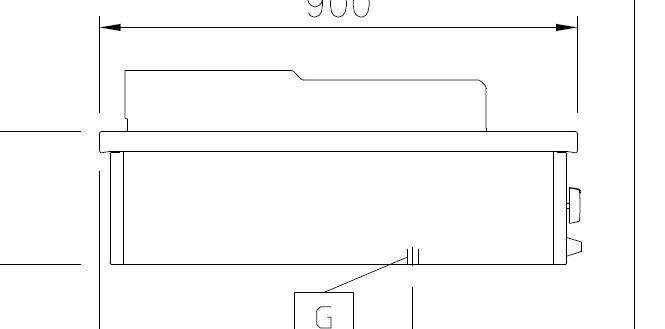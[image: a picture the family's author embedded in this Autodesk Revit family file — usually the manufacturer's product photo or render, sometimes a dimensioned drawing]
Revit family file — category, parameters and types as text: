
# Revit family: QF_ELECTROLUXPROFESSIONAL_589279_MCDAABDOPO
name_source: partatom
category: Specialty Equipment
revit_build: Autodesk Revit 2018 (Build: 20190510_1515(x64)
units: mm (PartAtom-declared; Revit-internal decimal feet)

## family parameters
Always vertical = Yes
Cut with Voids When Loaded = No
Part Type = Normal
Room Calculation Point = No
Round Connector Dimension = Use Diameter
Shared = No
Work Plane-Based = No

## types (1)
- QF_ELECTROLUXPROFESSIONAL_589279_MCDAABDOPO
    Description = GAS CHARGRILL,1SIDE,BACKSPL,400X900X250H
    Direct Waste Size = 0"
    Gas Connection Height = 0 mm  [stored 0 ft]
    Gas KW = 10.5
    Gas Size = 1"
    HP = 0 HP
    Manufacturer = ELECTROLUX
    Model = 589279
    Watts = 0 W
    Weight in Pounds = 143.3

note: [stored X ft] marks values corroborated as IEEE doubles in the binary element streams (Revit-internal decimal feet)

## geometry (parser evidence)
native form markers: Blend x27, Sweep x13
no freeform markers — native parametric forms only
